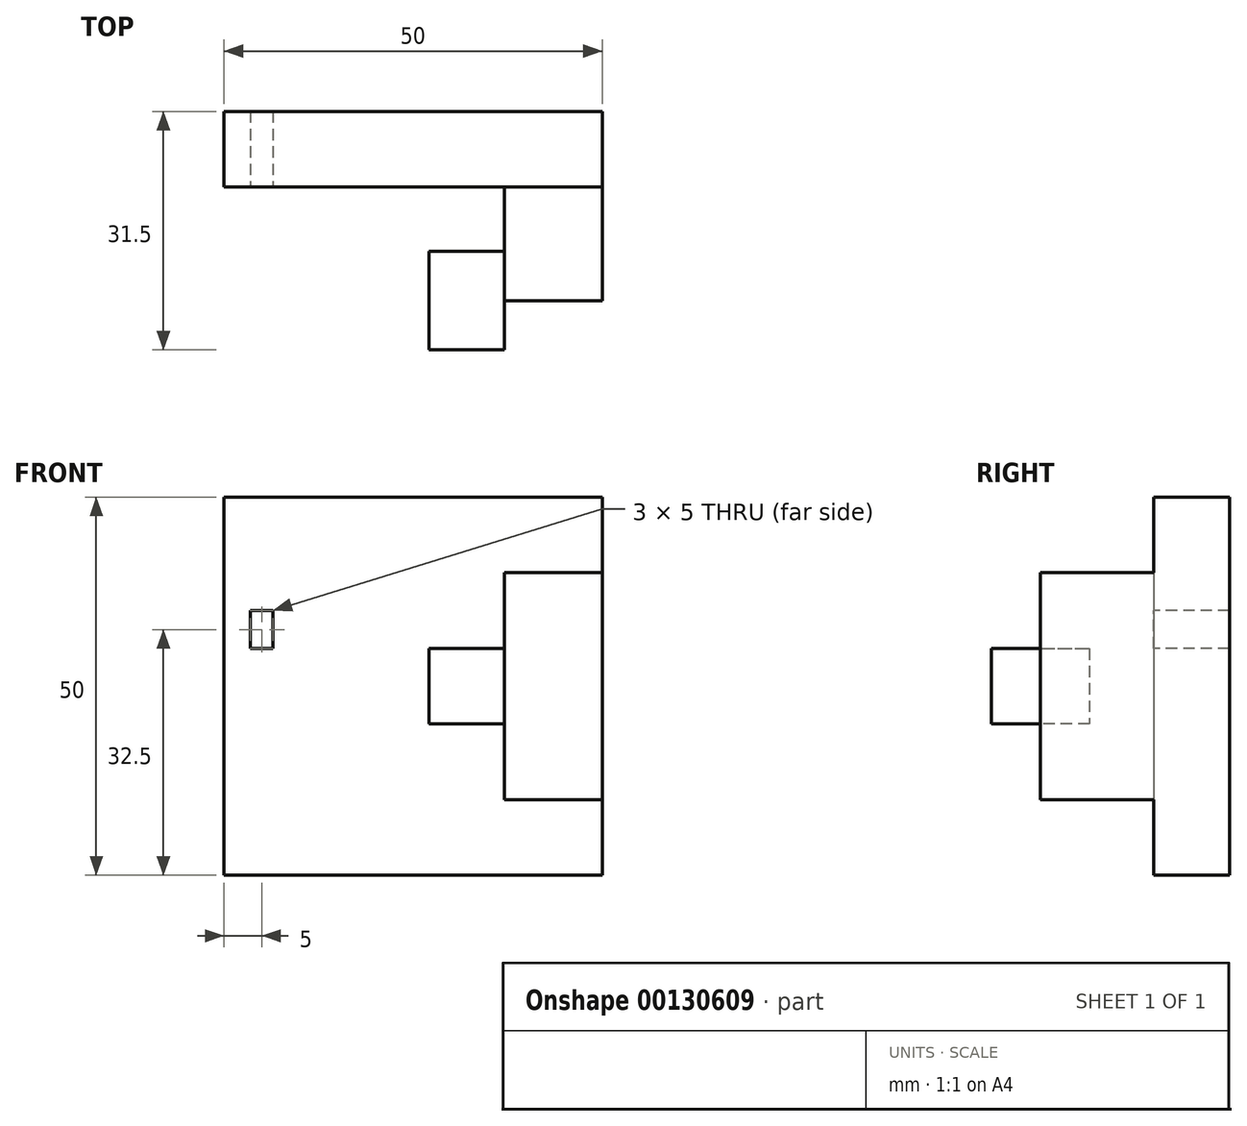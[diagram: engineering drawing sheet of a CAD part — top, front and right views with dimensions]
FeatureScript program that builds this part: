
annotation { "Feature Type Name" : "Feature", "Feature Type Description" : "" }
export const myFeature = defineFeature(function(context is Context, id is Id, definition is map)
    precondition{}
    {
        {
            var Q0;
            Q0=qCreatedBy(makeId("Front.planeOp"),FACE);
            var sketch = newSketch(context, id + "F0", { "sketchPlane" : qUnion([Q0])});
            skLineSegment(sketch, "E0.bottom", {"start": v(25, 25) * mm, "end": v(-25, 25) * mm});
            skLineSegment(sketch, "E0.top", {"start": v(25, -25) * mm, "end": v(-25, -25) * mm});
            skLineSegment(sketch, "E0.left", {"start": v(25, 25) * mm, "end": v(25, -25) * mm});
            skLineSegment(sketch, "E0.right", {"start": v(-25, 25) * mm, "end": v(-25, -25) * mm});
            skPoint(sketch, "E0.middle", {"position": v(0, 0) * mm});
            skLineSegment(sketch, "E1", {"start": v(25, 15) * mm, "end": v(12.1, 15) * mm});
            skLineSegment(sketch, "E2", {"start": v(12.1, 15) * mm, "end": v(12.1, -15) * mm});
            skLineSegment(sketch, "E3", {"start": v(12.1, -15) * mm, "end": v(25, -15) * mm});
            skLineSegment(sketch, "E4", {"start": v(-25, -15) * mm, "end": v(-12.1, -15) * mm});
            skLineSegment(sketch, "E5", {"start": v(-12.1, -15) * mm, "end": v(-12.1, 15) * mm});
            skLineSegment(sketch, "E6", {"start": v(-12.1, 15) * mm, "end": v(-25, 15) * mm});
            skSolve(sketch);
        }
        {
            var Q0;
            {var subQ0=sQuery(id+"F0.wireOp",EDGE,"E1");Q0=makeQuery(id+"F0.imprint","IMPRINT",FACE,{"disambiguationData":[TD([[makeQuery(id+"F0.imprint","IMPRINT",EDGE,{"derivedFrom":subQ0}),1.0]])]});}
            var Q1;
            {var subQ0=sQuery(id+"F0.wireOp",EDGE,"E4");Q1=makeQuery(id+"F0.imprint","IMPRINT",FACE,{"disambiguationData":[TD([[makeQuery(id+"F0.imprint","IMPRINT",EDGE,{"derivedFrom":subQ0}),1.0]])]});}
            extrude(context, id + "F1", {"entities" : qUnion([Q0, Q1]), "depth" : 25 * mm});
        }
        {
            var Q0;
            {var subQ4=sQuery(id+"F0.wireOp",EDGE,"E0.bottom");Q0=makeQuery(id+"F0.imprint","IMPRINT",FACE,{"disambiguationData":[TD([[makeQuery(id+"F0.imprint","IMPRINT",EDGE,{"derivedFrom":subQ4}),1.0]])]});}
            extrude(context, id + "F2", {"entities" : qUnion([Q0]), "operationType" : NewBodyOperationType.ADD, "depth" : 10 * mm});
        }
        {
            var Q0;
            Q0=makeQuery(id+"F1.opExtrude","SWEPT_FACE",FACE,{"disambiguationData":[OSD([sQuery(id+"F0.wireOp",EDGE,"E5")])]});
            var sketch = newSketch(context, id + "F3", { "sketchPlane" : qUnion([Q0])});
            skLineSegment(sketch, "E7", {"start": v(-25, 5) * mm, "end": v(-18.5, 5) * mm});
            skLineSegment(sketch, "E8", {"start": v(-18.5, 5) * mm, "end": v(-18.5, -5) * mm});
            skLineSegment(sketch, "E9", {"start": v(-18.5, -5) * mm, "end": v(-25, -5) * mm});
            skLineSegment(sketch, "E10", {"start": v(-10, 12.16) * mm, "end": v(-10, 1.89) * mm});
            skSolve(sketch);
        }
        {
            var Q0;
            Q0=qSketchRegion(id+"F3",true);
            var Q1;
            {var subQ0=sQuery(id+"F3.wireOp",EDGE,"E7");Q1=makeQuery(id+"F3.imprint","IMPRINT",FACE,{"disambiguationData":[TD([[makeQuery(id+"F3.imprint","IMPRINT",EDGE,{"derivedFrom":subQ0}),-1.0]])]});}
            extrude(context, id + "F4", {"entities" : qUnion([Q0, Q1]), "operationType" : NewBodyOperationType.ADD, "depth" : 10 * mm});
        }
        {
            var Q0;
            Q0=makeQuery(id+"F1.opExtrude","SWEPT_FACE",FACE,{"disambiguationData":[OSD([sQuery(id+"F0.wireOp",EDGE,"E2")])]});
            var sketch = newSketch(context, id + "F5", { "sketchPlane" : qUnion([Q0])});
            skLineSegment(sketch, "E11", {"start": v(25, 5) * mm, "end": v(18.5, 5) * mm});
            skLineSegment(sketch, "E12", {"start": v(18.5, 5) * mm, "end": v(18.5, -5) * mm});
            skLineSegment(sketch, "E13", {"start": v(18.5, -5) * mm, "end": v(25, -5) * mm});
            skSolve(sketch);
        }
        {
            var Q0;
            Q0=qSketchRegion(id+"F5",true);
            var Q1;
            {var subQ0=sQuery(id+"F5.wireOp",EDGE,"E11");Q1=makeQuery(id+"F5.imprint","IMPRINT",FACE,{"disambiguationData":[TD([[makeQuery(id+"F5.imprint","IMPRINT",EDGE,{"derivedFrom":subQ0}),1.0]])]});}
            extrude(context, id + "F6", {"entities" : qUnion([Q0, Q1]), "operationType" : NewBodyOperationType.ADD, "depth" : 10 * mm});
        }
        {
            var Q0;
            {var subQ0=sQuery(id+"F0.wireOp",EDGE,"E0.right");Q0=makeQuery(id+"F2.boolean.opBoolean","MERGE",FACE,{"derivedFrom":[makeQuery(id+"F1.opExtrude","SWEPT_FACE",FACE,{"disambiguationData":[OSD([subQ0])]}),makeQuery(id+"F2.opExtrude","SWEPT_FACE",FACE,{"disambiguationData":[OSD([subQ0]),TDD([makeQuery(id+"F0.imprint","IMPRINT",EDGE,{"disambiguationData":[TD([[makeQuery(id+"F0.imprint","INTERSECT",VERTEX,{"derivedFrom":[sQuery(id+"F0.wireOp",EDGE,"E0.bottom"),subQ0]}),-1.0]])],"derivedFrom":subQ0})])]}),makeQuery(id+"F2.opExtrude","SWEPT_FACE",FACE,{"disambiguationData":[OSD([subQ0]),TDD([makeQuery(id+"F0.imprint","IMPRINT",EDGE,{"disambiguationData":[TD([[makeQuery(id+"F0.imprint","INTERSECT",VERTEX,{"derivedFrom":[sQuery(id+"F0.wireOp",EDGE,"E0.top"),subQ0]}),1.0]])],"derivedFrom":subQ0})])]})]});}
            var sketch = newSketch(context, id + "F7", { "sketchPlane" : qUnion([Q0])});
            skLineSegment(sketch, "E14", {"start": v(10, 15) * mm, "end": v(10, -15) * mm});
            skSolve(sketch);
        }
        {
            var Q0;
            Q0=qSketchRegion(id+"F7",true);
            var Q1;
            Q1=makeQuery(id+"F7.imprint","IMPRINT",FACE,{"disambiguationData":[TD([[makeQuery(id+"F7.imprint","IMPRINT",EDGE,{"derivedFrom":sQuery(id+"F7.wireOp",EDGE,"E14")}),1.0]])]});
            var Q2;
            Q2=makeQuery(id+"F4.opExtrude","CAP_FACE",FACE,{"disambiguationData":[OSD([sQuery(id+"F0.wireOp",EDGE,"E5"),sQuery(id+"F3.wireOp",EDGE,"E7"),sQuery(id+"F3.wireOp",EDGE,"E8"),sQuery(id+"F3.wireOp",EDGE,"E9")])],"isStart":false});
            extrude(context, id + "F8", {"entities" : qUnion([Q0, Q1]), "operationType" : NewBodyOperationType.REMOVE, "endBound" : BoundingType.UP_TO_SURFACE, "oppositeDirection" : true, "endBoundEntityFace" : qUnion([Q2]), "depth" : 25 * mm});
        }
        {
            var Q0;
            {var subQ0=sQuery(id+"F0.wireOp",EDGE,"E2");Q0=makeQuery(id+"F6.boolean.opBoolean","MERGE",FACE,{"derivedFrom":[makeQuery(id+"F1.opExtrude","CAP_FACE",FACE,{"disambiguationData":[OSD([sQuery(id+"F0.wireOp",EDGE,"E0.left"),sQuery(id+"F0.wireOp",EDGE,"E1"),subQ0,sQuery(id+"F0.wireOp",EDGE,"E3")])],"isStart":false}),makeQuery(id+"F6.opExtrude","SWEPT_FACE",FACE,{"disambiguationData":[OSD([subQ0])]})]});}
            var sketch = newSketch(context, id + "F9", { "sketchPlane" : qUnion([Q0])});
            skLineSegment(sketch, "E15", {"start": v(12.1, 5) * mm, "end": v(12.1, -5) * mm});
            skSolve(sketch);
        }
        {
            var Q0;
            Q0=qSketchRegion(id+"F9",true);
            var Q1;
            Q1=makeQuery(id+"F9.imprint","IMPRINT",FACE,{"disambiguationData":[TD([[makeQuery(id+"F9.imprint","IMPRINT",EDGE,{"derivedFrom":sQuery(id+"F9.wireOp",EDGE,"E15")}),-1.0]])]});
            var Q2;
            Q2=makeQuery(id+"F8.boolean.opBoolean","MERGE",FACE,{"derivedFrom":[makeQuery(id+"F2.opExtrude","CAP_FACE",FACE,{"disambiguationData":[OSD([sQuery(id+"F0.wireOp",EDGE,"E0.bottom"),sQuery(id+"F0.wireOp",EDGE,"E0.top"),sQuery(id+"F0.wireOp",EDGE,"E0.left"),sQuery(id+"F0.wireOp",EDGE,"E0.right"),sQuery(id+"F0.wireOp",EDGE,"E1"),sQuery(id+"F0.wireOp",EDGE,"E2"),sQuery(id+"F0.wireOp",EDGE,"E3"),sQuery(id+"F0.wireOp",EDGE,"E4"),sQuery(id+"F0.wireOp",EDGE,"E5"),sQuery(id+"F0.wireOp",EDGE,"E6")])],"isStart":false}),makeQuery(id+"F8.opExtrude","SWEPT_FACE",FACE,{"disambiguationData":[OSD([sQuery(id+"F7.wireOp",EDGE,"E14")])]})]});
            extrude(context, id + "F10", {"entities" : qUnion([Q0, Q1]), "operationType" : NewBodyOperationType.ADD, "endBoundEntityFace" : qUnion([Q2]), "depth" : 6.5 * mm});
        }
        {
            var Q0;
            Q0=makeQuery(id+"F8.boolean.opBoolean","MERGE",FACE,{"derivedFrom":[makeQuery(id+"F2.opExtrude","CAP_FACE",FACE,{"disambiguationData":[OSD([sQuery(id+"F0.wireOp",EDGE,"E0.bottom"),sQuery(id+"F0.wireOp",EDGE,"E0.top"),sQuery(id+"F0.wireOp",EDGE,"E0.left"),sQuery(id+"F0.wireOp",EDGE,"E0.right"),sQuery(id+"F0.wireOp",EDGE,"E1"),sQuery(id+"F0.wireOp",EDGE,"E2"),sQuery(id+"F0.wireOp",EDGE,"E3"),sQuery(id+"F0.wireOp",EDGE,"E4"),sQuery(id+"F0.wireOp",EDGE,"E5"),sQuery(id+"F0.wireOp",EDGE,"E6")])],"isStart":false}),makeQuery(id+"F8.opExtrude","SWEPT_FACE",FACE,{"disambiguationData":[OSD([sQuery(id+"F7.wireOp",EDGE,"E14")])]})]});
            var sketch = newSketch(context, id + "F11", { "sketchPlane" : qUnion([Q0])});
            skLineSegment(sketch, "E16.bottom", {"start": v(-18.5, 5) * mm, "end": v(-21.5, 5) * mm});
            skLineSegment(sketch, "E16.top", {"start": v(-18.5, 10) * mm, "end": v(-21.5, 10) * mm});
            skLineSegment(sketch, "E16.left", {"start": v(-18.5, 5) * mm, "end": v(-18.5, 10) * mm});
            skLineSegment(sketch, "E16.right", {"start": v(-21.5, 5) * mm, "end": v(-21.5, 10) * mm});
            skPoint(sketch, "E16.middle", {"position": v(-20, 7.5) * mm});
            skSolve(sketch);
        }
        {
            var Q0;
            Q0=makeQuery(id+"F11.imprint","IMPRINT",FACE,{"disambiguationData":[TD([[makeQuery(id+"F11.imprint","IMPRINT",EDGE,{"derivedFrom":sQuery(id+"F11.wireOp",EDGE,"E16.bottom")}),-1.0]])]});
            extrude(context, id + "F12", {"entities" : qUnion([Q0]), "operationType" : NewBodyOperationType.REMOVE, "oppositeDirection" : true, "depth" : 10 * mm});
        }
    });
